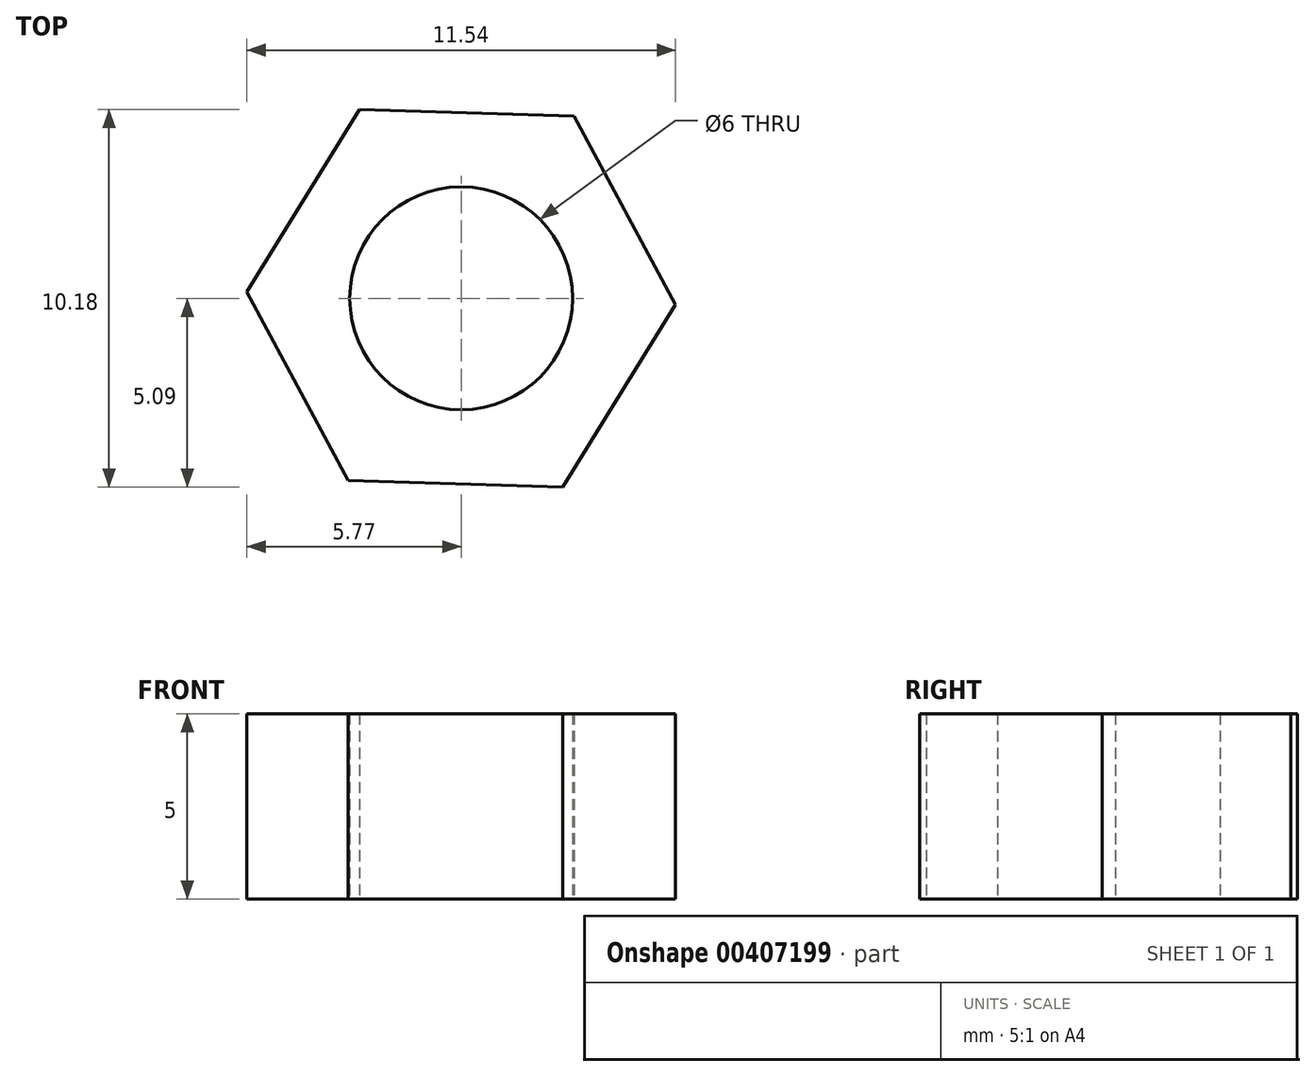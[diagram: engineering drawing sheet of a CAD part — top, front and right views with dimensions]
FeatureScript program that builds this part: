
annotation { "Feature Type Name" : "Feature", "Feature Type Description" : "" }
export const myFeature = defineFeature(function(context is Context, id is Id, definition is map)
    precondition{}
    {
        {
            var Q0;
            Q0=qCreatedBy(makeId("Top.planeOp"),FACE);
            var sketch = newSketch(context, id + "F0", { "sketchPlane" : qUnion([Q0])});
            skCircle(sketch, "E0", {"center": v(0, 0) * mm, "radius": 3 * mm});
            skCircle(sketch, "E1.cCircle", {"center": v(0, 0) * mm, "radius": 5 * mm, "construction": true});
            skLineSegment(sketch, "E1.0", {"start": v(5.77, -0.18) * mm, "end": v(2.73, -5.09) * mm});
            skLineSegment(sketch, "E1.1", {"start": v(2.73, -5.09) * mm, "end": v(-3.04, -4.9) * mm});
            skLineSegment(sketch, "E1.2", {"start": v(-3.04, -4.9) * mm, "end": v(-5.77, 0.18) * mm});
            skLineSegment(sketch, "E1.3", {"start": v(-5.77, 0.18) * mm, "end": v(-2.73, 5.09) * mm});
            skLineSegment(sketch, "E1.4", {"start": v(-2.73, 5.09) * mm, "end": v(3.04, 4.9) * mm});
            skLineSegment(sketch, "E1.5", {"start": v(3.04, 4.9) * mm, "end": v(5.77, -0.18) * mm});
            skPoint(sketch, "E1.0.midPoint", {"position": v(4.25, -2.63) * mm});
            skSolve(sketch);
        }
        {
            var Q0;
            Q0=makeQuery(id+"F0.imprint","IMPRINT",FACE,{"disambiguationData":[TD([[makeQuery(id+"F0.imprint","IMPRINT",EDGE,{"derivedFrom":sQuery(id+"F0.wireOp",EDGE,"E0")}),-1.0]])]});
            extrude(context, id + "F1", {"entities" : qUnion([Q0]), "depth" : 5 * mm});
        }
    });
